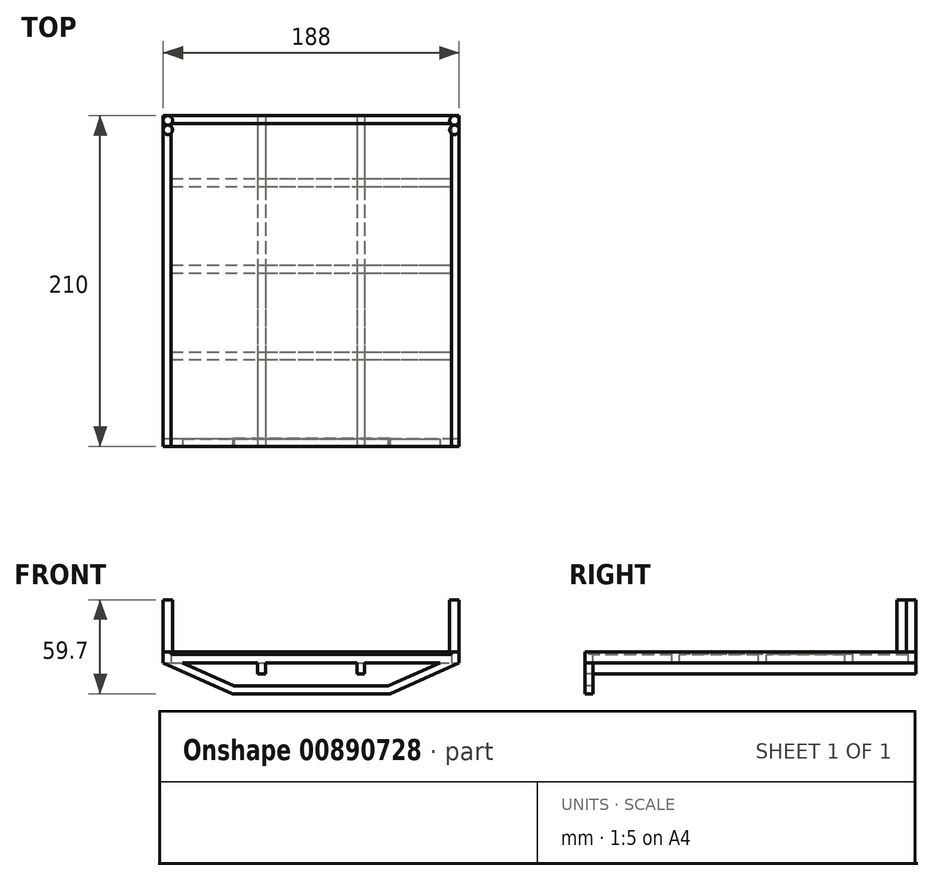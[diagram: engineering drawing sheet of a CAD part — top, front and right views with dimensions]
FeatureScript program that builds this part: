
annotation { "Feature Type Name" : "Feature", "Feature Type Description" : "" }
export const myFeature = defineFeature(function(context is Context, id is Id, definition is map)
    precondition{}
    {
        {
            var Q0;
            Q0=qCreatedBy(makeId("Top.planeOp"),FACE);
            var sketch = newSketch(context, id + "F0", { "sketchPlane" : qUnion([Q0])});
            skLineSegment(sketch, "E0.bottom", {"start": v(0, 0) * mm, "end": v(188, 0) * mm});
            skLineSegment(sketch, "E0.top", {"start": v(0, -210) * mm, "end": v(5, -210) * mm});
            skLineSegment(sketch, "E0.left", {"start": v(0, 0) * mm, "end": v(0, -210) * mm});
            skLineSegment(sketch, "E0.right", {"start": v(188, 0) * mm, "end": v(188, -210) * mm});
            skLineSegment(sketch, "E1.0", {"start": v(183, -5) * mm, "end": v(183, -210) * mm});
            skLineSegment(sketch, "E1.1", {"start": v(5, -5) * mm, "end": v(183, -5) * mm});
            skLineSegment(sketch, "E1.2", {"start": v(5, -5) * mm, "end": v(5, -210) * mm});
            skLineSegment(sketch, "E2.trimOffspring", {"start": v(183, -210) * mm, "end": v(188, -210) * mm});
            skSolve(sketch);
        }
        {
            var Q0;
            Q0 = qSketchRegion(id + "F0", true);
            extrude(context, id + "F1", {"entities" : qUnion([Q0]), "depth" : 7 * mm, "offsetDistance" : 25 * mm});
        }
        {
            var Q0;
            Q0=qCreatedBy(makeId("Top.planeOp"),FACE);
            var sketch = newSketch(context, id + "F2", { "sketchPlane" : qUnion([Q0])});
            skLineSegment(sketch, "E3.0", {"start": v(0, -210) * mm, "end": v(188, -210) * mm});
            skLineSegment(sketch, "E4.0", {"start": v(0, -205) * mm, "end": v(188, -205) * mm});
            skLineSegment(sketch, "E5", {"start": v(188, -210) * mm, "end": v(188, -205) * mm});
            skLineSegment(sketch, "E6", {"start": v(0, -210) * mm, "end": v(0, -205) * mm});
            skLineSegment(sketch, "E7.0", {"start": v(0, -155) * mm, "end": v(188, -155) * mm});
            skLineSegment(sketch, "E8.0", {"start": v(0, -150) * mm, "end": v(188, -150) * mm});
            skLineSegment(sketch, "E9.0", {"start": v(0, -100) * mm, "end": v(188, -100) * mm});
            skLineSegment(sketch, "E10.0", {"start": v(0, -95) * mm, "end": v(188, -95) * mm});
            skLineSegment(sketch, "E11.0", {"start": v(0, -45) * mm, "end": v(188, -45) * mm});
            skLineSegment(sketch, "E12.0", {"start": v(0, -40) * mm, "end": v(188, -40) * mm});
            skLineSegment(sketch, "E13", {"start": v(0, -40) * mm, "end": v(0, -45) * mm});
            skLineSegment(sketch, "E14", {"start": v(0, -95) * mm, "end": v(0, -100) * mm});
            skLineSegment(sketch, "E15", {"start": v(0, -150) * mm, "end": v(0, -155) * mm});
            skLineSegment(sketch, "E16", {"start": v(188, -40) * mm, "end": v(188, -45) * mm});
            skLineSegment(sketch, "E17", {"start": v(188, -95) * mm, "end": v(188, -100) * mm});
            skLineSegment(sketch, "E18", {"start": v(188, -150) * mm, "end": v(188, -155) * mm});
            skSolve(sketch);
        }
        {
            var Q0;
            Q0 = qSketchRegion(id + "F2", true);
            extrude(context, id + "F3", {"entities" : qUnion([Q0]), "operationType" : NewBodyOperationType.ADD, "depth" : 5 * mm, "offsetDistance" : 25 * mm});
        }
        {
            var Q0;
            Q0=qCreatedBy(makeId("Top.planeOp"),FACE);
            var sketch = newSketch(context, id + "F4", { "sketchPlane" : qUnion([Q0])});
            skLineSegment(sketch, "E19.0", {"start": v(60, 0) * mm, "end": v(60, -210) * mm});
            skLineSegment(sketch, "E20.0", {"start": v(65, 0) * mm, "end": v(65, -210) * mm});
            skLineSegment(sketch, "E21.0", {"start": v(128, 0) * mm, "end": v(128, -210) * mm});
            skLineSegment(sketch, "E22.0", {"start": v(123, 0) * mm, "end": v(123, -210) * mm});
            skLineSegment(sketch, "E23", {"start": v(60, 0) * mm, "end": v(65, 0) * mm});
            skLineSegment(sketch, "E24", {"start": v(123, 0) * mm, "end": v(128, 0) * mm});
            skLineSegment(sketch, "E25", {"start": v(123, -210) * mm, "end": v(128, -210) * mm});
            skLineSegment(sketch, "E26", {"start": v(65, -210) * mm, "end": v(60, -210) * mm});
            skSolve(sketch);
        }
        {
            var Q0;
            Q0 = qSketchRegion(id + "F4", true);
            extrude(context, id + "F5", {"entities" : qUnion([Q0]), "operationType" : NewBodyOperationType.ADD, "oppositeDirection" : true, "depth" : 7 * mm, "offsetDistance" : 25 * mm});
        }
        {
            var Q0;
            Q0=makeQuery(id+"F3.opExtrude","CAP_FACE",FACE,{"disambiguationData":[OSD([sQuery(id+"F2.wireOp",EDGE,"E3.0"),sQuery(id+"F2.wireOp",EDGE,"E4.0"),sQuery(id+"F2.wireOp",EDGE,"E5"),sQuery(id+"F2.wireOp",EDGE,"E6")])],"isStart":false});
            var sketch = newSketch(context, id + "F6", { "sketchPlane" : qUnion([Q0])});
            skLineSegment(sketch, "E27.bottom", {"start": v(0, 0) * mm, "end": v(188, 0) * mm});
            skLineSegment(sketch, "E27.top", {"start": v(0, -210) * mm, "end": v(188, -210) * mm});
            skLineSegment(sketch, "E27.left", {"start": v(0, 0) * mm, "end": v(0, -210) * mm});
            skLineSegment(sketch, "E27.right", {"start": v(188, 0) * mm, "end": v(188, -210) * mm});
            skSolve(sketch);
        }
        {
            var Q0;
            Q0 = qSketchRegion(id + "F6", true);
            extrude(context, id + "F7", {"entities" : qUnion([Q0]), "operationType" : NewBodyOperationType.ADD, "depth" : 0.2 * mm, "offsetDistance" : 25 * mm});
        }
        {
            var Q0;
            Q0=makeQuery(id+"F7.boolean.opBoolean","MERGE",FACE,{"derivedFrom":[makeQuery(id+"F5.boolean.opBoolean","MERGE",FACE,{"derivedFrom":[makeQuery(id+"F3.boolean.opBoolean","MERGE",FACE,{"derivedFrom":[makeQuery(id+"F1.opExtrude","SWEPT_FACE",FACE,{"disambiguationData":[OSD([sQuery(id+"F0.wireOp",EDGE,"E0.top")])]}),makeQuery(id+"F1.opExtrude","SWEPT_FACE",FACE,{"disambiguationData":[OSD([sQuery(id+"F0.wireOp",EDGE,"E2.trimOffspring")])]}),makeQuery(id+"F3.opExtrude","SWEPT_FACE",FACE,{"disambiguationData":[OSD([sQuery(id+"F2.wireOp",EDGE,"E3.0")])]})]}),makeQuery(id+"F5.opExtrude","SWEPT_FACE",FACE,{"disambiguationData":[OSD([sQuery(id+"F4.wireOp",EDGE,"E25")])]}),makeQuery(id+"F5.opExtrude","SWEPT_FACE",FACE,{"disambiguationData":[OSD([sQuery(id+"F4.wireOp",EDGE,"E26")])]})]}),makeQuery(id+"F7.opExtrude","SWEPT_FACE",FACE,{"disambiguationData":[OSD([sQuery(id+"F6.wireOp",EDGE,"E27.top")])]})]});
            var sketch = newSketch(context, id + "F8", { "sketchPlane" : qUnion([Q0])});
            skLineSegment(sketch, "E28", {"start": v(94, -19.7) * mm, "end": v(44, -19.7) * mm});
            skLineSegment(sketch, "E29.MirrorCS", {"start": v(94, -19.7) * mm, "end": v(144, -19.7) * mm});
            skLineSegment(sketch, "E30", {"start": v(0, 0) * mm, "end": v(44, -19.7) * mm});
            skLineSegment(sketch, "E31", {"start": v(144, -19.7) * mm, "end": v(188, 0) * mm});
            skLineSegment(sketch, "E32.0", {"start": v(0, 5) * mm, "end": v(188, 5) * mm});
            skLineSegment(sketch, "E33", {"start": v(0, 5) * mm, "end": v(0, 0) * mm});
            skLineSegment(sketch, "E34", {"start": v(188, 0) * mm, "end": v(188, 5) * mm});
            skLineSegment(sketch, "E35.0", {"start": v(142.93, -14.7) * mm, "end": v(175.76, 0) * mm});
            skLineSegment(sketch, "E35.1", {"start": v(12.24, 0) * mm, "end": v(175.76, 0) * mm});
            skLineSegment(sketch, "E35.2", {"start": v(94, -14.7) * mm, "end": v(142.93, -14.7) * mm});
            skLineSegment(sketch, "E35.3", {"start": v(94, -14.7) * mm, "end": v(45.07, -14.7) * mm});
            skLineSegment(sketch, "E35.4", {"start": v(12.24, 0) * mm, "end": v(45.07, -14.7) * mm});
            skSolve(sketch);
        }
        {
            var Q0;
            Q0 = qSketchRegion(id + "F8", true);
            extrude(context, id + "F9", {"entities" : qUnion([Q0]), "operationType" : NewBodyOperationType.ADD, "oppositeDirection" : true, "depth" : 5 * mm, "offsetDistance" : 25 * mm});
        }
        {
            var Q0;
            Q0 = qSketchRegion(id + "F8", true);
            extrude(context, id + "F10", {"entities" : qUnion([Q0]), "operationType" : NewBodyOperationType.ADD, "oppositeDirection" : true, "depth" : 5 * mm, "offsetDistance" : 25 * mm});
        }
        {
            var Q0;
            Q0=makeQuery(id+"F9.boolean.opBoolean","MERGE",FACE,{"derivedFrom":[makeQuery(id+"F3.opExtrude","SWEPT_FACE",FACE,{"disambiguationData":[OSD([sQuery(id+"F2.wireOp",EDGE,"E4.0")])]}),makeQuery(id+"F9.opExtrude","CAP_FACE",FACE,{"disambiguationData":[OSD([sQuery(id+"F8.wireOp",EDGE,"E28"),sQuery(id+"F8.wireOp",EDGE,"E29.MirrorCS"),sQuery(id+"F8.wireOp",EDGE,"E30"),sQuery(id+"F8.wireOp",EDGE,"E31"),sQuery(id+"F8.wireOp",EDGE,"E32.0"),sQuery(id+"F8.wireOp",EDGE,"E33"),sQuery(id+"F8.wireOp",EDGE,"E34"),sQuery(id+"F8.wireOp",EDGE,"E35.0"),sQuery(id+"F8.wireOp",EDGE,"E35.1"),sQuery(id+"F8.wireOp",EDGE,"E35.2"),sQuery(id+"F8.wireOp",EDGE,"E35.3"),sQuery(id+"F8.wireOp",EDGE,"E35.4")])],"isStart":false})]});
            var sketch = newSketch(context, id + "F11", { "sketchPlane" : qUnion([Q0])});
            skLineSegment(sketch, "E36", {"start": v(-188, 0) * mm, "end": v(-144, -19.7) * mm});
            skLineSegment(sketch, "E37", {"start": v(-144, -19.7) * mm, "end": v(-44, -19.7) * mm});
            skLineSegment(sketch, "E38", {"start": v(-44, -19.7) * mm, "end": v(0, 0) * mm});
            skLineSegment(sketch, "E39", {"start": v(0, 0) * mm, "end": v(-188, 0) * mm});
            skSolve(sketch);
        }
        {
            var Q0;
            Q0 = qSketchRegion(id + "F11", true);
            extrude(context, id + "F12", {"entities" : qUnion([Q0]), "operationType" : NewBodyOperationType.ADD, "oppositeDirection" : true, "depth" : 0.2 * mm, "offsetDistance" : 25 * mm});
        }
        {
            var Q0;
            Q0=qCreatedBy(makeId("Top.planeOp"),FACE);
            var sketch = newSketch(context, id + "F13", { "sketchPlane" : qUnion([Q0])});
            skCircle(sketch, "E40", {"center": v(3, -3) * mm, "radius": 3 * mm});
            skCircle(sketch, "E41", {"center": v(3, -9) * mm, "radius": 3 * mm});
            skCircle(sketch, "E42.MirrorC", {"center": v(185, -9) * mm, "radius": 3 * mm});
            skCircle(sketch, "E43.MirrorC", {"center": v(185, -3) * mm, "radius": 3 * mm});
            skSolve(sketch);
        }
        {
            var Q0;
            Q0 = qSketchRegion(id + "F13", true);
            extrude(context, id + "F14", {"entities" : qUnion([Q0]), "operationType" : NewBodyOperationType.ADD, "depth" : 40 * mm, "offsetDistance" : 25 * mm, "hasSecondDirection" : true, "secondDirectionOppositeDirection" : false, "secondDirectionDepth" : 7 * mm});
        }
    });
